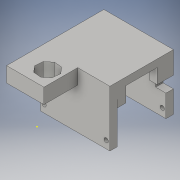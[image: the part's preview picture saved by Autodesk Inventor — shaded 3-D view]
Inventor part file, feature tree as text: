
AUTODESK INVENTOR PART (.ipt)
format: ipt  version: 2016 (Build 200138000, 138)  size: 231,936 bytes
history: native  units: in
note: dims shown in document units (in); Inventor stores cm internally (conversion verified against a paired STEP export)
features: sketch x10, extrude x9
ambient origin geometry x8: Origin, YZ Plane, XZ Plane, XY Plane, X Axis, Y Axis, Z Axis, Center Point
bodies: Solid1 (feature_tree)
feature tree (19):
  extrude  "Extrusion1"  Depth=1.264in
  extrude  "Extrusion2"  Depth=0.25in
  extrude  "Extrusion3"  Depth=2.148in
  extrude  "Extrusion4"  Depth=0.25in
  extrude  "Extrusion5"  Depth=0.25in
  extrude  "Extrusion6"  Depth=1.648in
  extrude  "Extrusion7"  Depth=0.25in
  extrude  "Extrusion8"  Depth=0.25in
  sketch  "Sketch9"  dims[d21=2.355in d22=1.3885in d23=0.0in]
  extrude  "Extrusion9"  Depth=1.3885in TaperAngle=0.0deg
  sketch  "Sketch1"  dims[d0=1.1438in d1=1.264in]
  sketch  "Sketch2"  dims[d5=0.65in d6=0.25in]
  sketch  "Sketch3"  dims[d8=2.3545in d9=2.148in]
  sketch  "Sketch4"  dims[d10=2.3545in d11=0.25in]
  sketch  "Sketch5"  dims[d12=0.5in d13=0.25in]
  sketch  "Sketch6"  dims[d14=1.8545in d15=1.648in]
  sketch  "Sketch7"  dims[d16=0.25in d17=0.25in]
  sketch  "Sketch8"  dims[d18=0.5115in d19=0.0in d20=0.25in]
  sketch  "Sketch10"  dims[d24=0.5115in d25=0.0in d26=2.355in d27=0.5115in d28=1.9in d29=0.0in d30=1.3885in d31=0.0in d37=0.25in d38=0.0in d39=0.35in d40=0.75in d41=0.75in d42=1.6875in d43=0.0in d44=0.2615in d45=0.0in d52=5.824in d53=0.0in]
